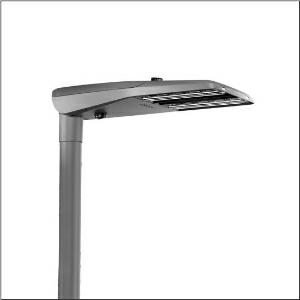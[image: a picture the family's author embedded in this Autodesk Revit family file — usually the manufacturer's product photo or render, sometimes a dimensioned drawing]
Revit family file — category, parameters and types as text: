
# Revit family: streetlight_sl_11_iq_midi___pc-l_5xc3e51y08me_36d5
name_source: partatom
category: Lighting Fixtures
units: mm (PartAtom-declared; Revit-internal decimal feet)

## family parameters
Cut with Voids When Loaded = No
Host = Face
Light Source = No
Part Type = Normal
Room Calculation Point = No
Round Connector Dimension = Use Diameter
Shared = No

## types (1)
- --- (1 x LED, 15540 lm, 122.7 W, 3000K)
    Apparent Load = 123 VA
    CIE Flux Codes = 37 73 96 100 100
    Color Rendering = 70
    Color Temperature = 3000K
    Default Elevation = 1800 mm
    Description = Streetlight SL 11 iQ midi, mast luminaire, primary light control with 3 zone facetted reflector, of plastic, silver coated, highly specular, primary optical cover: cover, of PMMA, transparent, light distribution: PC-L, light emission: direct distribution, primary light characteristic: asymmetric, left, installation type: post-top, side-entry, lamps: LED, High Power LED, rated values: 15.540lm | 122,7W | 126,7lm/W (begin service life); end service life: 15.540lm | 130,2W; at 50% lumin. flux: 7.770lm | 56,1W | 138,5lm/W, colour temperature: 3000K, colour rendering: CRI > 70, light colour: 730, light setting 1 begin service life: 100% | 15.540lm | 122,7W | 126,7lm/W | 3.000K, light setting 1 end service life: 130,2W, further light settings possible, control: pre-setting: logarithmic dimming characteristic, Street-Remote, Auto-Match, Temp-Guard, Lumen-Switch, Night-Set, Smart-Wire, Light-Fading, Desk-Remote (wireless, voltage-free reading and setting of iQ features in the workshop via application-optimized NFC function/RFID function), optimised constant luminous flux control (CLO 2.0), with cable H07RN-F 5x 1.5mm², mains connection: 230..240V, AC, 50/60Hz, connection cable pre-assembled, cable length: 12,5m, luminaire housing, of diecast aluminium, powder-coated, Siteco® metallic grey (DB 702S), please order mast flange separately, inclination adjustable without tools: 0°, 5°, 10°, 15° (post-top) | 0°, -5°, -10°, -15° (side-entry), sealing non-destructively replaceable, multi-level sealing system, length: 780mm, width: 376mm, height: 118mm, mast flange for spigot size: 42mm (side-entry): 5XC10008XM4, 60/48mm (side-entry/post-top): 5XC10108XM2, 76/60mm (side-entry/post-top): 5XC10108XM1, equipment: Power, Smart Interface below and above, protection rating (complete): IP66, insulation class (complete): insulation class II (safety insulation), certification: CE, ENEC, ENEC+, VDE, UKCA, impact resistance: IK10, permissible operating ambient temperature for outdoor applications: -25..+50°C, standard-compliant lighting for roads and squares, Environmental Product Declaration (EPD) tested and certified by an independent institute, packaging unit: 1 piece

Light Distribution: PC-L
    Height = 118 mm
    Lamp = 1 x LED
    Lamp Light Flux = 15540 lm
    Lamp Power = 122.7 W
    Lamp count = 1
    Length = 780 mm
    Luminous efficacy = 127 lm/W
    Manufacturer = Siteco
    ModVariant = No
    Model = 5XC3E51Y08ME
    Number of Poles = 1
    OnlyDefault = Yes
    Power Factor = 1
    Product Name = Streetlight SL 11 iQ midi | PC-L
    Product group = mast luminaire | pylon top
    ProductGroupID = 6100
    Protection Class = Protection class II
    Protection Degree = IP 66
    RLX_Detail_Level = 1
    RLX_Emergency_Light_Flux = 0 lm
    RLX_Emergency_Type = 0
    RLX_Emergency_Type_DB = No
    RlxData = <blob elided: 73721 chars, md5=48627862>
    Socket = socket
    Standby Power = 0 W
    System Light Flux = 15540 lm
    System Power = 123 W
    Type Comments = factory setting: luminous flux: 100 % | dim-lin: 254 | 552 mA
    Type Image = l_1004429.jpg
    URL = http://relux.com
    VarID = @adj_154479
    Voltage = 0 V
    Weight = 0.00 kg
    Width = 376 mm

## geometry (parser evidence)
native form markers: Blend x4, Sweep x11
no freeform markers — native parametric forms only
